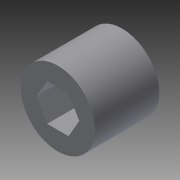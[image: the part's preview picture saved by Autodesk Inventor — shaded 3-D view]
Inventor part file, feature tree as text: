
AUTODESK INVENTOR PART (.ipt)
format: ipt  version: 2014 SP1 (Build 180222100, 222)  size: 82,944 bytes
history: native  units: in
note: dims shown in document units (in); Inventor stores cm internally (conversion verified against a paired STEP export)
features: extrude x1, sketch x1
ambient origin geometry x8: Origin, YZ Plane, XZ Plane, XY Plane, X Axis, Y Axis, Z Axis, Center Point
bodies: Solid1 (feature_tree)
feature tree (2):
  extrude  "Extrusion1"  Depth=0.866in
  sketch  "Sketch1"  dims[d0=0.25in d1=1.0in d2=0.866in d3=0.0in]
